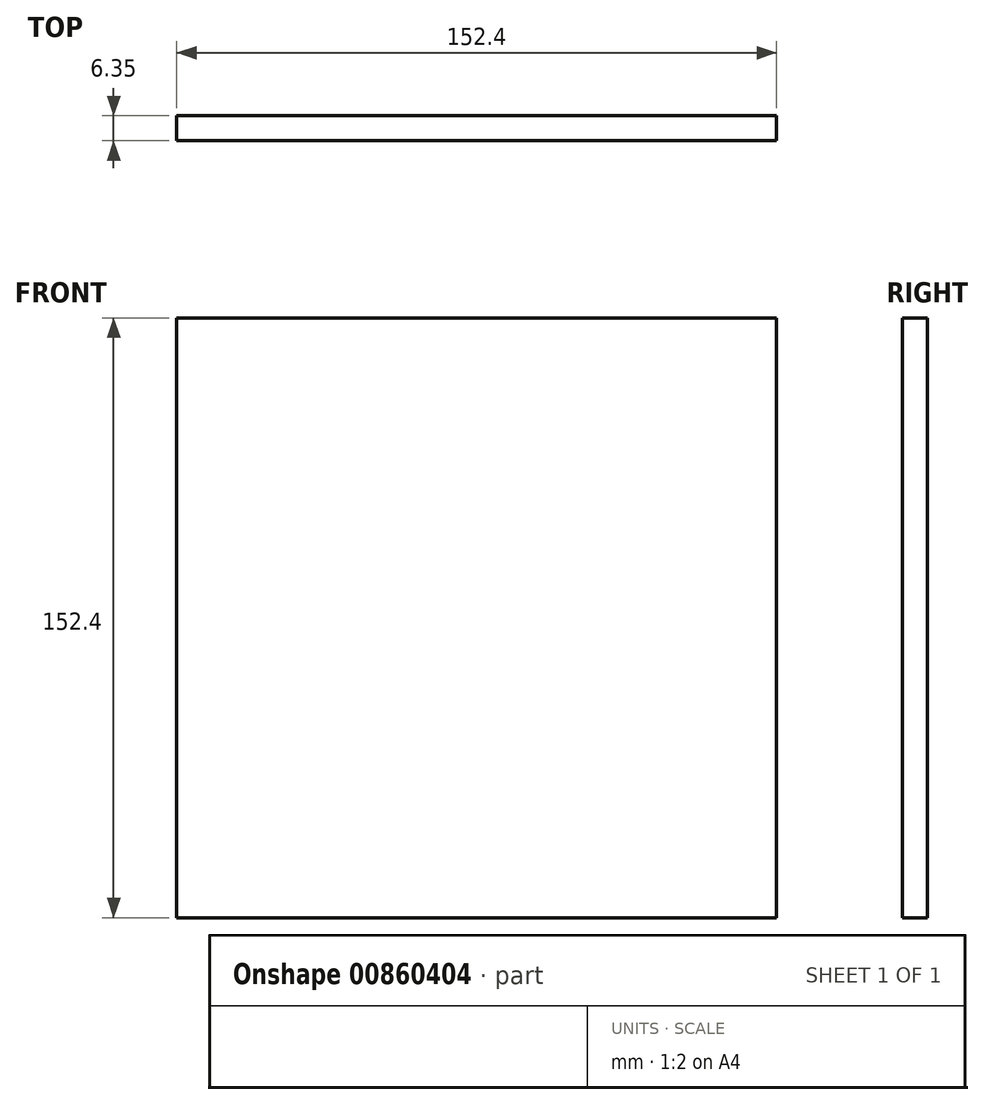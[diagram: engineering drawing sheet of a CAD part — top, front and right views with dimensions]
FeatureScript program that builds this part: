
annotation { "Feature Type Name" : "Feature", "Feature Type Description" : "" }
export const myFeature = defineFeature(function(context is Context, id is Id, definition is map)
    precondition{}
    {
        {
            var Q0;
            Q0=qCreatedBy(makeId("Front.planeOp"),FACE);
            var sketch = newSketch(context, id + "F0", { "sketchPlane" : qUnion([Q0])});
            skLineSegment(sketch, "E0.bottom", {"start": v(0, 0) * mm, "end": v(152.4, 0) * mm});
            skLineSegment(sketch, "E0.top", {"start": v(0, 152.4) * mm, "end": v(152.4, 152.4) * mm});
            skLineSegment(sketch, "E0.left", {"start": v(0, 0) * mm, "end": v(0, 152.4) * mm});
            skLineSegment(sketch, "E0.right", {"start": v(152.4, 0) * mm, "end": v(152.4, 152.4) * mm});
            skSolve(sketch);
        }
        {
            var Q0;
            Q0 = qSketchRegion(id + "F0", true);
            extrude(context, id + "F1", {"entities" : qUnion([Q0]), "depth" : 6.35 * mm, "offsetDistance" : 25.4 * mm});
        }
    });
